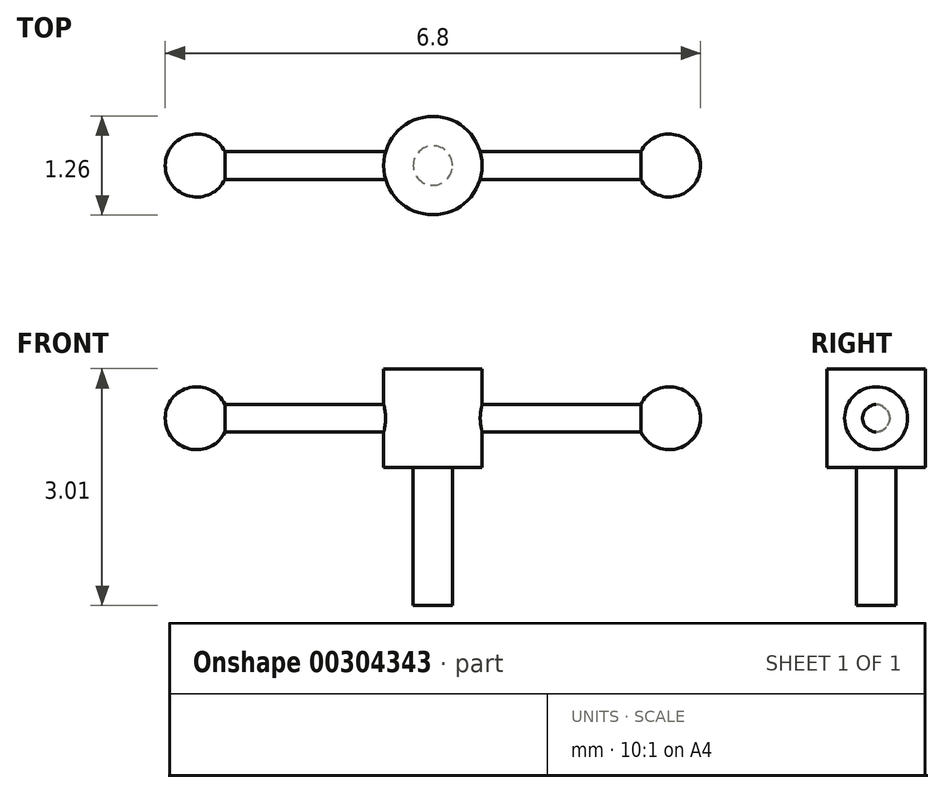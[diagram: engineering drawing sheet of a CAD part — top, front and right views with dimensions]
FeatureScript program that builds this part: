
annotation { "Feature Type Name" : "Feature", "Feature Type Description" : "" }
export const myFeature = defineFeature(function(context is Context, id is Id, definition is map)
    precondition{}
    {
        {
            var Q0;
            Q0=qCreatedBy(makeId("Front.planeOp"),FACE);
            var sketch = newSketch(context, id + "F0", { "sketchPlane" : qUnion([Q0])});
            skPoint(sketch, "E0.startSnap0", {"position": v(32, 0) * mm});
            skLineSegment(sketch, "E1", {"start": v(-3, 0) * mm, "end": v(3, 0) * mm});
            skLineSegment(sketch, "E2", {"start": v(-3, 0) * mm, "end": v(-3.4, 0) * mm});
            skArc(sketch, "E3", {"start": v(-3.4, 0) * mm, "mid": v(-3, 0.4) * mm, "end": v(-2.6, 0) * mm});
            skLineSegment(sketch, "E4", {"start": v(3, 0) * mm, "end": v(3.4, 0) * mm});
            skArc(sketch, "E5", {"start": v(3.4, 0) * mm, "mid": v(3, 0.4) * mm, "end": v(2.6, 0) * mm});
            skSolve(sketch);
        }
        {
            var Q0;
            Q0=qCreatedBy(makeId("Right.planeOp"),FACE);
            var sketch = newSketch(context, id + "F1", { "sketchPlane" : qUnion([Q0])});
            skCircle(sketch, "E6", {"center": v(0, 0) * mm, "radius": 0.17 * mm});
            skSolve(sketch);
        }
        {
            var Q0;
            {var subQ0=sQuery(id+"F0.wireOp",EDGE,"E2");Q0=makeQuery(id+"F0.imprint","IMPRINT",FACE,{"disambiguationData":[TD([[makeQuery(id+"F0.imprint","IMPRINT",EDGE,{"derivedFrom":subQ0}),-1.0]])]});}
            var Q1;
            Q1=sQuery(id+"F0.wireOp",EDGE,"E2");
            revolve(context, id + "F2", {"entities" : qUnion([Q0]), "axis" : qUnion([Q1]), "revolveType" : RevolveType.FULL});
        }
        {
            var Q0;
            {var subQ0=sQuery(id+"F0.wireOp",EDGE,"E2");Q0=makeQuery(id+"F0.imprint","IMPRINT",FACE,{"disambiguationData":[TD([[makeQuery(id+"F0.imprint","IMPRINT",EDGE,{"derivedFrom":subQ0}),-1.0]])]});}
            var Q1;
            {var subQ0=sQuery(id+"F0.wireOp",EDGE,"E4");Q1=makeQuery(id+"F0.imprint","IMPRINT",FACE,{"disambiguationData":[TD([[makeQuery(id+"F0.imprint","IMPRINT",EDGE,{"derivedFrom":subQ0}),1.0]])]});}
            var Q2;
            Q2=sQuery(id+"F0.wireOp",EDGE,"E4");
            revolve(context, id + "F3", {"entities" : qUnion([Q0, Q1]), "axis" : qUnion([Q2]), "revolveType" : RevolveType.FULL});
        }
        {
            var Q0;
            Q0=makeQuery(id+"F1.imprint","IMPRINT",FACE,{"disambiguationData":[TD([[makeQuery(id+"F1.imprint","IMPRINT",EDGE,{"derivedFrom":sQuery(id+"F1.wireOp",EDGE,"E6")}),1.0]])]});
            extrude(context, id + "F4", {"entities" : qUnion([Q0]), "operationType" : NewBodyOperationType.ADD, "endBound" : BoundingType.SYMMETRIC, "depth" : 6 * mm});
        }
        {
            var Q0;
            Q0=qCreatedBy(makeId("Top.planeOp"),FACE);
            cPlane(context, id + "F5", {"entities" : qUnion([Q0]), "cplaneType" : CPlaneType.OFFSET, "offset" : .625 * mm, "width" : 150 * mm, "height" : 150 * mm});
        }
        {
            var Q0;
            Q0=qCreatedBy(id+"F5.planeOp",FACE);
            var sketch = newSketch(context, id + "F6", { "sketchPlane" : qUnion([Q0])});
            skCircle(sketch, "E7", {"center": v(0, 0) * mm, "radius": 0.62 * mm});
            skSolve(sketch);
        }
        {
            var Q0;
            Q0 = qSketchRegion(id + "F6", true);
            extrude(context, id + "F7", {"entities" : qUnion([Q0]), "operationType" : NewBodyOperationType.ADD, "oppositeDirection" : true, "depth" : 1.25 * mm});
        }
        {
            var Q0;
            Q0=makeQuery(id+"F7.opExtrude","CAP_FACE",FACE,{"disambiguationData":[OSD([sQuery(id+"F6.wireOp",EDGE,"E7")])],"isStart":false});
            var sketch = newSketch(context, id + "F8", { "sketchPlane" : qUnion([Q0])});
            skCircle(sketch, "E8", {"center": v(0, 0) * mm, "radius": 0.25 * mm});
            skSolve(sketch);
        }
        {
            var Q0;
            Q0 = qSketchRegion(id + "F8", true);
            extrude(context, id + "F9", {"entities" : qUnion([Q0]), "operationType" : NewBodyOperationType.ADD, "depth" : (3 - 1.25) * mm});
        }
    });
